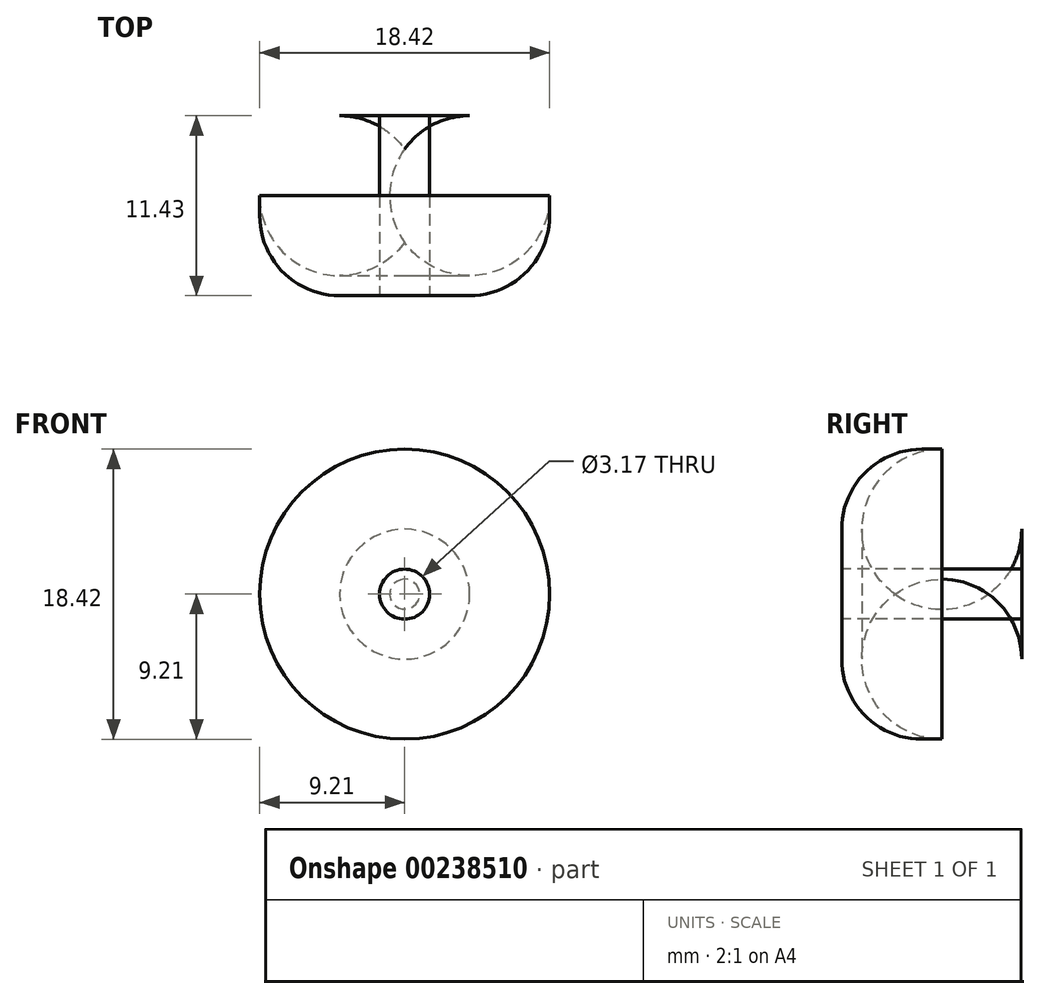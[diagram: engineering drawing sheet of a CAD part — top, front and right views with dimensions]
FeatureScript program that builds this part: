
annotation { "Feature Type Name" : "Feature", "Feature Type Description" : "" }
export const myFeature = defineFeature(function(context is Context, id is Id, definition is map)
    precondition{}
    {
        {
            var Q0;
            Q0=qCreatedBy(makeId("Front.planeOp"),FACE);
            var sketch = newSketch(context, id + "F0", { "sketchPlane" : qUnion([Q0])});
            skCircle(sketch, "E0", {"center": v(0, 0) * mm, "radius": 9.2 * mm});
            skSolve(sketch);
        }
        {
            var Q0;
            Q0=makeQuery(id+"F0.imprint","IMPRINT",FACE,{"disambiguationData":[TD([[makeQuery(id+"F0.imprint","IMPRINT",EDGE,{"derivedFrom":sQuery(id+"F0.wireOp",EDGE,"E0")}),1.0]])]});
            extrude(context, id + "F1", {"entities" : qUnion([Q0]), "depth" : 11.43 * mm});
        }
        {
            var Q0;
            Q0=makeQuery(id+"F1.opExtrude","CAP_EDGE",EDGE,{"disambiguationData":[OSD([sQuery(id+"F0.wireOp",EDGE,"E0")])],"isStart":false});
            var Q1;
            Q1=makeQuery(id+"F1.opExtrude","CAP_EDGE",EDGE,{"disambiguationData":[OSD([sQuery(id+"F0.wireOp",EDGE,"E0")])],"isStart":true});
            fillet(context, id + "F2", {"entities" : qUnion([Q0, Q1]), "radius" : 5.08 * mm, "tangentPropagation" : true, "allowEdgeOverflow" : false});
        }
        {
            var Q0;
            Q0=makeQuery(id+"F1.opExtrude","CAP_FACE",FACE,{"disambiguationData":[OSD([sQuery(id+"F0.wireOp",EDGE,"E0")])],"isStart":false});
            var sketch = newSketch(context, id + "F3", { "sketchPlane" : qUnion([Q0])});
            skCircle(sketch, "E1", {"center": v(0, 0) * mm, "radius": 1.59 * mm});
            skSolve(sketch);
        }
        {
            var Q0;
            Q0=makeQuery(id+"F3.imprint","IMPRINT",FACE,{"disambiguationData":[TD([[makeQuery(id+"F3.imprint","IMPRINT",EDGE,{"derivedFrom":sQuery(id+"F3.wireOp",EDGE,"E1")}),1.0]])]});
            extrude(context, id + "F4", {"entities" : qUnion([Q0]), "operationType" : NewBodyOperationType.REMOVE, "oppositeDirection" : true, "depth" : 25.4 * mm});
        }
    });
